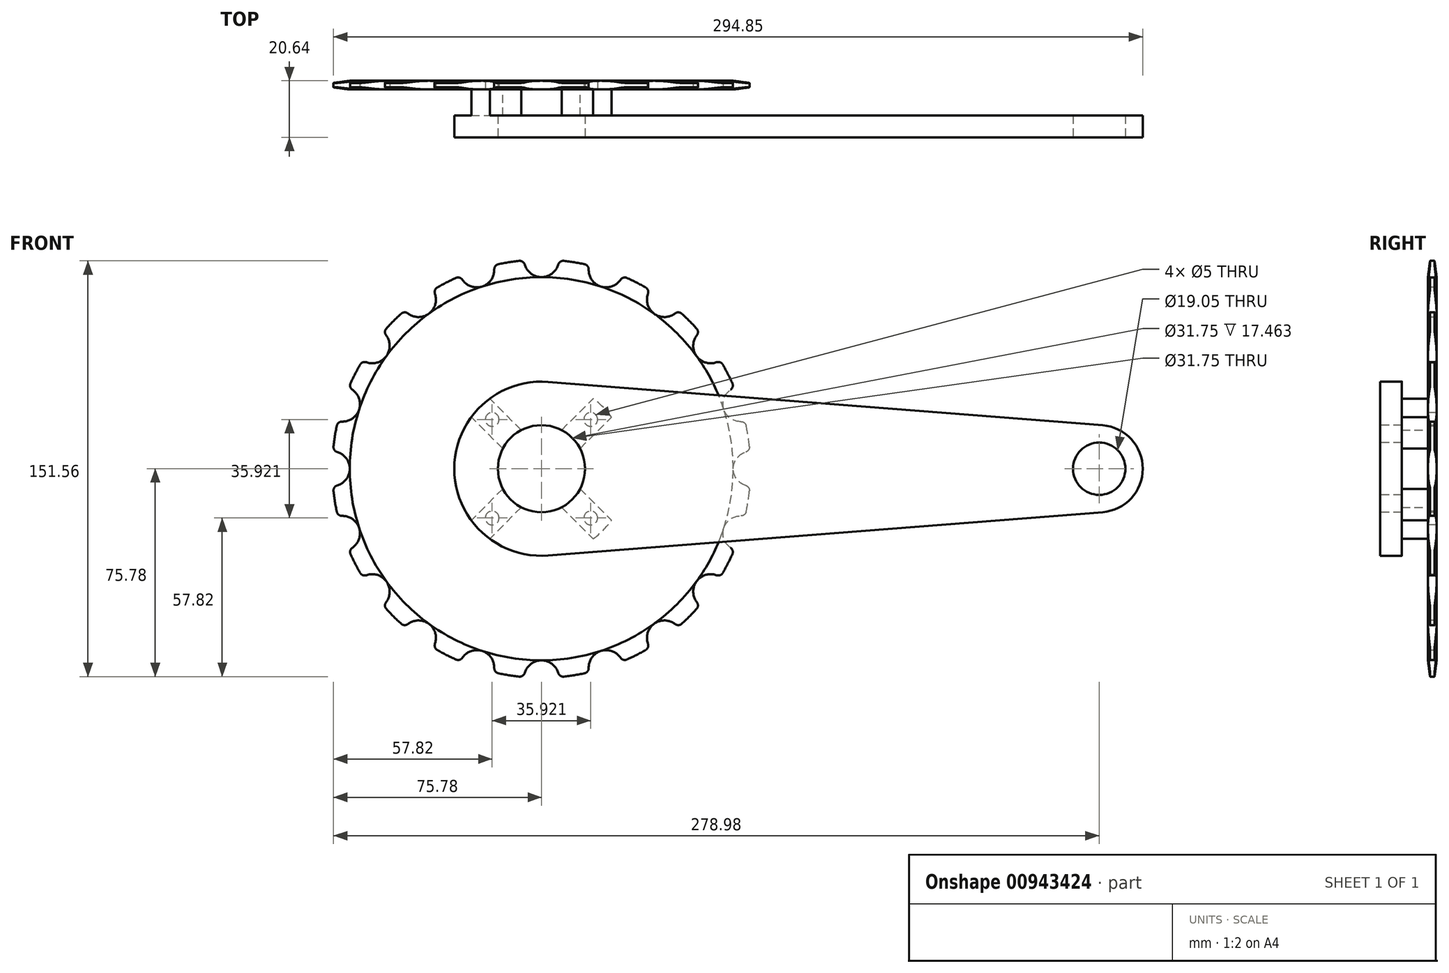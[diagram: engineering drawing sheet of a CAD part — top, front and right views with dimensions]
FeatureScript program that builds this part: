
annotation { "Feature Type Name" : "Feature", "Feature Type Description" : "" }
export const myFeature = defineFeature(function(context is Context, id is Id, definition is map)
    precondition{}
    {
        {
            var Q0;
            Q0=qCreatedBy(makeId("Right.planeOp"),FACE);
            var sketch = newSketch(context, id + "F0", { "sketchPlane" : qUnion([Q0])});
            skLineSegment(sketch, "E0.left", {"start": v(-1.59, 69.85) * mm, "end": v(-1.59, 0) * mm});
            skLineSegment(sketch, "E0.right", {"start": v(1.59, 69.85) * mm, "end": v(1.59, 0) * mm});
            skPoint(sketch, "E0.middle", {"position": v(0, 0) * mm});
            skLineSegment(sketch, "E1", {"start": v(0, 0) * mm, "end": v(-39.14, 0) * mm, "construction": true});
            skLineSegment(sketch, "E2", {"start": v(-1.59, 0) * mm, "end": v(1.59, 0) * mm});
            skLineSegment(sketch, "E3", {"start": v(-1.59, 69.85) * mm, "end": v(-0.8, 76.2) * mm});
            skLineSegment(sketch, "E4", {"start": v(0, 76.2) * mm, "end": v(0, 0) * mm, "construction": true});
            skLineSegment(sketch, "E5.MirrorCS", {"start": v(1.59, 69.85) * mm, "end": v(0.8, 76.2) * mm});
            skLineSegment(sketch, "E6", {"start": v(0.8, 76.2) * mm, "end": v(0, 76.2) * mm});
            skLineSegment(sketch, "E7", {"start": v(-0.8, 76.2) * mm, "end": v(0, 76.2) * mm});
            skSolve(sketch);
        }
        {
            var Q0;
            Q0 = qSketchRegion(id + "F0", true);
            var Q1;
            Q1=sQuery(id+"F0.wireOp",EDGE,"E1");
            revolve(context, id + "F1", {"surfaceOperationType" : NewSurfaceOperationType.NEW, "entities" : qUnion([Q0]), "axis" : qUnion([Q1]), "revolveType" : RevolveType.FULL});
        }
        {
            var Q0;
            Q0=qCreatedBy(makeId("Front.planeOp"),FACE);
            var sketch = newSketch(context, id + "F2", { "sketchPlane" : qUnion([Q0])});
            skCircle(sketch, "E8", {"center": v(0, 76.2) * mm, "radius": 6.35 * mm});
            skCircle(sketch, "E9.1.0", {"center": v(-23.55, 72.47) * mm, "radius": 6.35 * mm});
            skCircle(sketch, "E9.2.0", {"center": v(-44.79, 61.65) * mm, "radius": 6.35 * mm});
            skCircle(sketch, "E9.3.0", {"center": v(-61.65, 44.79) * mm, "radius": 6.35 * mm});
            skCircle(sketch, "E9.4.0", {"center": v(-72.47, 23.55) * mm, "radius": 6.35 * mm});
            skCircle(sketch, "E9.5.0", {"center": v(-76.2, 0) * mm, "radius": 6.35 * mm});
            skCircle(sketch, "E9.6.0", {"center": v(-72.47, -23.55) * mm, "radius": 6.35 * mm});
            skCircle(sketch, "E9.7.0", {"center": v(-61.65, -44.79) * mm, "radius": 6.35 * mm});
            skCircle(sketch, "E9.8.0", {"center": v(-44.79, -61.65) * mm, "radius": 6.35 * mm});
            skCircle(sketch, "E9.9.0", {"center": v(-23.55, -72.47) * mm, "radius": 6.35 * mm});
            skCircle(sketch, "E9.10.0", {"center": v(0, -76.2) * mm, "radius": 6.35 * mm});
            skCircle(sketch, "E9.11.0", {"center": v(23.55, -72.47) * mm, "radius": 6.35 * mm});
            skCircle(sketch, "E9.12.0", {"center": v(44.79, -61.65) * mm, "radius": 6.35 * mm});
            skCircle(sketch, "E9.13.0", {"center": v(61.65, -44.79) * mm, "radius": 6.35 * mm});
            skCircle(sketch, "E9.14.0", {"center": v(72.47, -23.55) * mm, "radius": 6.35 * mm});
            skCircle(sketch, "E9.15.0", {"center": v(76.2, 0) * mm, "radius": 6.35 * mm});
            skCircle(sketch, "E9.16.0", {"center": v(72.47, 23.55) * mm, "radius": 6.35 * mm});
            skCircle(sketch, "E9.17.0", {"center": v(61.65, 44.79) * mm, "radius": 6.35 * mm});
            skCircle(sketch, "E9.18.0", {"center": v(44.79, 61.65) * mm, "radius": 6.35 * mm});
            skCircle(sketch, "E9.19.0", {"center": v(23.55, 72.47) * mm, "radius": 6.35 * mm});
            skPoint(sketch, "E9.center", {"position": v(0, 0) * mm});
            skSolve(sketch);
        }
        {
            var Q0;
            Q0 = qSketchRegion(id + "F2", true);
            extrude(context, id + "F3", {"entities" : qUnion([Q0]), "operationType" : NewBodyOperationType.REMOVE, "endBound" : BoundingType.THROUGH_ALL, "oppositeDirection" : true, "depth" : 25.4 * mm, "offsetDistance" : 25.4 * mm, "hasSecondDirection" : true, "secondDirectionBound" : SecondDirectionBoundingType.THROUGH_ALL, "secondDirectionOppositeDirection" : false, "secondDirectionDepth" : 25.4 * mm});
        }
        {
            var Q0;
            Q0=makeQuery(id+"F3.boolean.opBoolean","INTERSECT",EDGE,{"disambiguationData":[OD(0.0)],"derivedFrom":[makeQuery(id+"F1.opRevolve","SWEPT_FACE",FACE,{"disambiguationData":[OSD([sQuery(id+"F0.wireOp",EDGE,"E6"),sQuery(id+"F0.wireOp",EDGE,"E7")])]}),makeQuery(id+"F3.opExtrude","SWEPT_FACE",FACE,{"disambiguationData":[OSD([sQuery(id+"F2.wireOp",EDGE,"E9.1.0")])]})]});
            var Q1;
            Q1=makeQuery(id+"F3.boolean.opBoolean","INTERSECT",EDGE,{"disambiguationData":[OD(0.0)],"derivedFrom":[makeQuery(id+"F1.opRevolve","SWEPT_FACE",FACE,{"disambiguationData":[OSD([sQuery(id+"F0.wireOp",EDGE,"E6"),sQuery(id+"F0.wireOp",EDGE,"E7")])]}),makeQuery(id+"F3.opExtrude","SWEPT_FACE",FACE,{"disambiguationData":[OSD([sQuery(id+"F2.wireOp",EDGE,"E8")])]})]});
            var Q2;
            Q2=makeQuery(id+"F3.boolean.opBoolean","INTERSECT",EDGE,{"disambiguationData":[OD(1.0)],"derivedFrom":[makeQuery(id+"F1.opRevolve","SWEPT_FACE",FACE,{"disambiguationData":[OSD([sQuery(id+"F0.wireOp",EDGE,"E6"),sQuery(id+"F0.wireOp",EDGE,"E7")])]}),makeQuery(id+"F3.opExtrude","SWEPT_FACE",FACE,{"disambiguationData":[OSD([sQuery(id+"F2.wireOp",EDGE,"E9.1.0")])]})]});
            var Q3;
            Q3=makeQuery(id+"F3.boolean.opBoolean","INTERSECT",EDGE,{"disambiguationData":[OD(0.0)],"derivedFrom":[makeQuery(id+"F1.opRevolve","SWEPT_FACE",FACE,{"disambiguationData":[OSD([sQuery(id+"F0.wireOp",EDGE,"E6"),sQuery(id+"F0.wireOp",EDGE,"E7")])]}),makeQuery(id+"F3.opExtrude","SWEPT_FACE",FACE,{"disambiguationData":[OSD([sQuery(id+"F2.wireOp",EDGE,"E9.2.0")])]})]});
            var Q4;
            Q4=makeQuery(id+"F3.boolean.opBoolean","INTERSECT",EDGE,{"disambiguationData":[OD(0.0)],"derivedFrom":[makeQuery(id+"F1.opRevolve","SWEPT_FACE",FACE,{"disambiguationData":[OSD([sQuery(id+"F0.wireOp",EDGE,"E6"),sQuery(id+"F0.wireOp",EDGE,"E7")])]}),makeQuery(id+"F3.opExtrude","SWEPT_FACE",FACE,{"disambiguationData":[OSD([sQuery(id+"F2.wireOp",EDGE,"E9.19.0")])]})]});
            var Q5;
            Q5=makeQuery(id+"F3.boolean.opBoolean","INTERSECT",EDGE,{"disambiguationData":[OD(1.0)],"derivedFrom":[makeQuery(id+"F1.opRevolve","SWEPT_FACE",FACE,{"disambiguationData":[OSD([sQuery(id+"F0.wireOp",EDGE,"E6"),sQuery(id+"F0.wireOp",EDGE,"E7")])]}),makeQuery(id+"F3.opExtrude","SWEPT_FACE",FACE,{"disambiguationData":[OSD([sQuery(id+"F2.wireOp",EDGE,"E8")])]})]});
            var Q6;
            Q6=makeQuery(id+"F3.boolean.opBoolean","INTERSECT",EDGE,{"disambiguationData":[OD(1.0)],"derivedFrom":[makeQuery(id+"F1.opRevolve","SWEPT_FACE",FACE,{"disambiguationData":[OSD([sQuery(id+"F0.wireOp",EDGE,"E6"),sQuery(id+"F0.wireOp",EDGE,"E7")])]}),makeQuery(id+"F3.opExtrude","SWEPT_FACE",FACE,{"disambiguationData":[OSD([sQuery(id+"F2.wireOp",EDGE,"E9.19.0")])]})]});
            var Q7;
            Q7=makeQuery(id+"F3.boolean.opBoolean","INTERSECT",EDGE,{"disambiguationData":[OD(1.0)],"derivedFrom":[makeQuery(id+"F1.opRevolve","SWEPT_FACE",FACE,{"disambiguationData":[OSD([sQuery(id+"F0.wireOp",EDGE,"E6"),sQuery(id+"F0.wireOp",EDGE,"E7")])]}),makeQuery(id+"F3.opExtrude","SWEPT_FACE",FACE,{"disambiguationData":[OSD([sQuery(id+"F2.wireOp",EDGE,"E9.18.0")])]})]});
            var Q8;
            Q8=makeQuery(id+"F3.boolean.opBoolean","INTERSECT",EDGE,{"disambiguationData":[OD(0.0)],"derivedFrom":[makeQuery(id+"F1.opRevolve","SWEPT_FACE",FACE,{"disambiguationData":[OSD([sQuery(id+"F0.wireOp",EDGE,"E6"),sQuery(id+"F0.wireOp",EDGE,"E7")])]}),makeQuery(id+"F3.opExtrude","SWEPT_FACE",FACE,{"disambiguationData":[OSD([sQuery(id+"F2.wireOp",EDGE,"E9.18.0")])]})]});
            var Q9;
            Q9=makeQuery(id+"F3.boolean.opBoolean","INTERSECT",EDGE,{"disambiguationData":[OD(1.0)],"derivedFrom":[makeQuery(id+"F1.opRevolve","SWEPT_FACE",FACE,{"disambiguationData":[OSD([sQuery(id+"F0.wireOp",EDGE,"E6"),sQuery(id+"F0.wireOp",EDGE,"E7")])]}),makeQuery(id+"F3.opExtrude","SWEPT_FACE",FACE,{"disambiguationData":[OSD([sQuery(id+"F2.wireOp",EDGE,"E9.17.0")])]})]});
            var Q10;
            Q10=makeQuery(id+"F3.boolean.opBoolean","INTERSECT",EDGE,{"disambiguationData":[OD(0.0)],"derivedFrom":[makeQuery(id+"F1.opRevolve","SWEPT_FACE",FACE,{"disambiguationData":[OSD([sQuery(id+"F0.wireOp",EDGE,"E6"),sQuery(id+"F0.wireOp",EDGE,"E7")])]}),makeQuery(id+"F3.opExtrude","SWEPT_FACE",FACE,{"disambiguationData":[OSD([sQuery(id+"F2.wireOp",EDGE,"E9.17.0")])]})]});
            var Q11;
            Q11=makeQuery(id+"F3.boolean.opBoolean","INTERSECT",EDGE,{"disambiguationData":[OD(1.0)],"derivedFrom":[makeQuery(id+"F1.opRevolve","SWEPT_FACE",FACE,{"disambiguationData":[OSD([sQuery(id+"F0.wireOp",EDGE,"E6"),sQuery(id+"F0.wireOp",EDGE,"E7")])]}),makeQuery(id+"F3.opExtrude","SWEPT_FACE",FACE,{"disambiguationData":[OSD([sQuery(id+"F2.wireOp",EDGE,"E9.2.0")])]})]});
            var Q12;
            Q12=makeQuery(id+"F3.boolean.opBoolean","INTERSECT",EDGE,{"disambiguationData":[OD(0.0)],"derivedFrom":[makeQuery(id+"F1.opRevolve","SWEPT_FACE",FACE,{"disambiguationData":[OSD([sQuery(id+"F0.wireOp",EDGE,"E6"),sQuery(id+"F0.wireOp",EDGE,"E7")])]}),makeQuery(id+"F3.opExtrude","SWEPT_FACE",FACE,{"disambiguationData":[OSD([sQuery(id+"F2.wireOp",EDGE,"E9.3.0")])]})]});
            var Q13;
            Q13=makeQuery(id+"F3.boolean.opBoolean","INTERSECT",EDGE,{"disambiguationData":[OD(1.0)],"derivedFrom":[makeQuery(id+"F1.opRevolve","SWEPT_FACE",FACE,{"disambiguationData":[OSD([sQuery(id+"F0.wireOp",EDGE,"E6"),sQuery(id+"F0.wireOp",EDGE,"E7")])]}),makeQuery(id+"F3.opExtrude","SWEPT_FACE",FACE,{"disambiguationData":[OSD([sQuery(id+"F2.wireOp",EDGE,"E9.3.0")])]})]});
            var Q14;
            Q14=makeQuery(id+"F3.boolean.opBoolean","INTERSECT",EDGE,{"disambiguationData":[OD(1.0)],"derivedFrom":[makeQuery(id+"F1.opRevolve","SWEPT_FACE",FACE,{"disambiguationData":[OSD([sQuery(id+"F0.wireOp",EDGE,"E6"),sQuery(id+"F0.wireOp",EDGE,"E7")])]}),makeQuery(id+"F3.opExtrude","SWEPT_FACE",FACE,{"disambiguationData":[OSD([sQuery(id+"F2.wireOp",EDGE,"E9.4.0")])]})]});
            var Q15;
            Q15=makeQuery(id+"F3.boolean.opBoolean","INTERSECT",EDGE,{"disambiguationData":[OD(1.0)],"derivedFrom":[makeQuery(id+"F1.opRevolve","SWEPT_FACE",FACE,{"disambiguationData":[OSD([sQuery(id+"F0.wireOp",EDGE,"E6"),sQuery(id+"F0.wireOp",EDGE,"E7")])]}),makeQuery(id+"F3.opExtrude","SWEPT_FACE",FACE,{"disambiguationData":[OSD([sQuery(id+"F2.wireOp",EDGE,"E9.5.0")])]})]});
            var Q16;
            Q16=makeQuery(id+"F3.boolean.opBoolean","INTERSECT",EDGE,{"disambiguationData":[OD(0.0)],"derivedFrom":[makeQuery(id+"F1.opRevolve","SWEPT_FACE",FACE,{"disambiguationData":[OSD([sQuery(id+"F0.wireOp",EDGE,"E6"),sQuery(id+"F0.wireOp",EDGE,"E7")])]}),makeQuery(id+"F3.opExtrude","SWEPT_FACE",FACE,{"disambiguationData":[OSD([sQuery(id+"F2.wireOp",EDGE,"E9.5.0")])]})]});
            var Q17;
            Q17=makeQuery(id+"F3.boolean.opBoolean","INTERSECT",EDGE,{"disambiguationData":[OD(0.0)],"derivedFrom":[makeQuery(id+"F1.opRevolve","SWEPT_FACE",FACE,{"disambiguationData":[OSD([sQuery(id+"F0.wireOp",EDGE,"E6"),sQuery(id+"F0.wireOp",EDGE,"E7")])]}),makeQuery(id+"F3.opExtrude","SWEPT_FACE",FACE,{"disambiguationData":[OSD([sQuery(id+"F2.wireOp",EDGE,"E9.4.0")])]})]});
            var Q18;
            Q18=makeQuery(id+"F3.boolean.opBoolean","INTERSECT",EDGE,{"disambiguationData":[OD(0.0)],"derivedFrom":[makeQuery(id+"F1.opRevolve","SWEPT_FACE",FACE,{"disambiguationData":[OSD([sQuery(id+"F0.wireOp",EDGE,"E6"),sQuery(id+"F0.wireOp",EDGE,"E7")])]}),makeQuery(id+"F3.opExtrude","SWEPT_FACE",FACE,{"disambiguationData":[OSD([sQuery(id+"F2.wireOp",EDGE,"E9.6.0")])]})]});
            var Q19;
            Q19=makeQuery(id+"F3.boolean.opBoolean","INTERSECT",EDGE,{"disambiguationData":[OD(1.0)],"derivedFrom":[makeQuery(id+"F1.opRevolve","SWEPT_FACE",FACE,{"disambiguationData":[OSD([sQuery(id+"F0.wireOp",EDGE,"E6"),sQuery(id+"F0.wireOp",EDGE,"E7")])]}),makeQuery(id+"F3.opExtrude","SWEPT_FACE",FACE,{"disambiguationData":[OSD([sQuery(id+"F2.wireOp",EDGE,"E9.6.0")])]})]});
            var Q20;
            Q20=makeQuery(id+"F3.boolean.opBoolean","INTERSECT",EDGE,{"disambiguationData":[OD(0.0)],"derivedFrom":[makeQuery(id+"F1.opRevolve","SWEPT_FACE",FACE,{"disambiguationData":[OSD([sQuery(id+"F0.wireOp",EDGE,"E6"),sQuery(id+"F0.wireOp",EDGE,"E7")])]}),makeQuery(id+"F3.opExtrude","SWEPT_FACE",FACE,{"disambiguationData":[OSD([sQuery(id+"F2.wireOp",EDGE,"E9.7.0")])]})]});
            var Q21;
            Q21=makeQuery(id+"F3.boolean.opBoolean","INTERSECT",EDGE,{"disambiguationData":[OD(1.0)],"derivedFrom":[makeQuery(id+"F1.opRevolve","SWEPT_FACE",FACE,{"disambiguationData":[OSD([sQuery(id+"F0.wireOp",EDGE,"E6"),sQuery(id+"F0.wireOp",EDGE,"E7")])]}),makeQuery(id+"F3.opExtrude","SWEPT_FACE",FACE,{"disambiguationData":[OSD([sQuery(id+"F2.wireOp",EDGE,"E9.7.0")])]})]});
            var Q22;
            Q22=makeQuery(id+"F3.boolean.opBoolean","INTERSECT",EDGE,{"disambiguationData":[OD(0.0)],"derivedFrom":[makeQuery(id+"F1.opRevolve","SWEPT_FACE",FACE,{"disambiguationData":[OSD([sQuery(id+"F0.wireOp",EDGE,"E6"),sQuery(id+"F0.wireOp",EDGE,"E7")])]}),makeQuery(id+"F3.opExtrude","SWEPT_FACE",FACE,{"disambiguationData":[OSD([sQuery(id+"F2.wireOp",EDGE,"E9.8.0")])]})]});
            var Q23;
            Q23=makeQuery(id+"F3.boolean.opBoolean","INTERSECT",EDGE,{"disambiguationData":[OD(1.0)],"derivedFrom":[makeQuery(id+"F1.opRevolve","SWEPT_FACE",FACE,{"disambiguationData":[OSD([sQuery(id+"F0.wireOp",EDGE,"E6"),sQuery(id+"F0.wireOp",EDGE,"E7")])]}),makeQuery(id+"F3.opExtrude","SWEPT_FACE",FACE,{"disambiguationData":[OSD([sQuery(id+"F2.wireOp",EDGE,"E9.8.0")])]})]});
            var Q24;
            Q24=makeQuery(id+"F3.boolean.opBoolean","INTERSECT",EDGE,{"disambiguationData":[OD(0.0)],"derivedFrom":[makeQuery(id+"F1.opRevolve","SWEPT_FACE",FACE,{"disambiguationData":[OSD([sQuery(id+"F0.wireOp",EDGE,"E6"),sQuery(id+"F0.wireOp",EDGE,"E7")])]}),makeQuery(id+"F3.opExtrude","SWEPT_FACE",FACE,{"disambiguationData":[OSD([sQuery(id+"F2.wireOp",EDGE,"E9.9.0")])]})]});
            var Q25;
            Q25=makeQuery(id+"F3.boolean.opBoolean","INTERSECT",EDGE,{"disambiguationData":[OD(1.0)],"derivedFrom":[makeQuery(id+"F1.opRevolve","SWEPT_FACE",FACE,{"disambiguationData":[OSD([sQuery(id+"F0.wireOp",EDGE,"E6"),sQuery(id+"F0.wireOp",EDGE,"E7")])]}),makeQuery(id+"F3.opExtrude","SWEPT_FACE",FACE,{"disambiguationData":[OSD([sQuery(id+"F2.wireOp",EDGE,"E9.9.0")])]})]});
            var Q26;
            Q26=makeQuery(id+"F3.boolean.opBoolean","INTERSECT",EDGE,{"disambiguationData":[OD(0.0)],"derivedFrom":[makeQuery(id+"F1.opRevolve","SWEPT_FACE",FACE,{"disambiguationData":[OSD([sQuery(id+"F0.wireOp",EDGE,"E6"),sQuery(id+"F0.wireOp",EDGE,"E7")])]}),makeQuery(id+"F3.opExtrude","SWEPT_FACE",FACE,{"disambiguationData":[OSD([sQuery(id+"F2.wireOp",EDGE,"E9.10.0")])]})]});
            var Q27;
            Q27=makeQuery(id+"F3.boolean.opBoolean","INTERSECT",EDGE,{"disambiguationData":[OD(1.0)],"derivedFrom":[makeQuery(id+"F1.opRevolve","SWEPT_FACE",FACE,{"disambiguationData":[OSD([sQuery(id+"F0.wireOp",EDGE,"E6"),sQuery(id+"F0.wireOp",EDGE,"E7")])]}),makeQuery(id+"F3.opExtrude","SWEPT_FACE",FACE,{"disambiguationData":[OSD([sQuery(id+"F2.wireOp",EDGE,"E9.10.0")])]})]});
            var Q28;
            Q28=makeQuery(id+"F3.boolean.opBoolean","INTERSECT",EDGE,{"disambiguationData":[OD(0.0)],"derivedFrom":[makeQuery(id+"F1.opRevolve","SWEPT_FACE",FACE,{"disambiguationData":[OSD([sQuery(id+"F0.wireOp",EDGE,"E6"),sQuery(id+"F0.wireOp",EDGE,"E7")])]}),makeQuery(id+"F3.opExtrude","SWEPT_FACE",FACE,{"disambiguationData":[OSD([sQuery(id+"F2.wireOp",EDGE,"E9.11.0")])]})]});
            var Q29;
            Q29=makeQuery(id+"F3.boolean.opBoolean","INTERSECT",EDGE,{"disambiguationData":[OD(1.0)],"derivedFrom":[makeQuery(id+"F1.opRevolve","SWEPT_FACE",FACE,{"disambiguationData":[OSD([sQuery(id+"F0.wireOp",EDGE,"E6"),sQuery(id+"F0.wireOp",EDGE,"E7")])]}),makeQuery(id+"F3.opExtrude","SWEPT_FACE",FACE,{"disambiguationData":[OSD([sQuery(id+"F2.wireOp",EDGE,"E9.11.0")])]})]});
            var Q30;
            Q30=makeQuery(id+"F3.boolean.opBoolean","INTERSECT",EDGE,{"disambiguationData":[OD(0.0)],"derivedFrom":[makeQuery(id+"F1.opRevolve","SWEPT_FACE",FACE,{"disambiguationData":[OSD([sQuery(id+"F0.wireOp",EDGE,"E6"),sQuery(id+"F0.wireOp",EDGE,"E7")])]}),makeQuery(id+"F3.opExtrude","SWEPT_FACE",FACE,{"disambiguationData":[OSD([sQuery(id+"F2.wireOp",EDGE,"E9.12.0")])]})]});
            var Q31;
            Q31=makeQuery(id+"F3.boolean.opBoolean","INTERSECT",EDGE,{"disambiguationData":[OD(1.0)],"derivedFrom":[makeQuery(id+"F1.opRevolve","SWEPT_FACE",FACE,{"disambiguationData":[OSD([sQuery(id+"F0.wireOp",EDGE,"E6"),sQuery(id+"F0.wireOp",EDGE,"E7")])]}),makeQuery(id+"F3.opExtrude","SWEPT_FACE",FACE,{"disambiguationData":[OSD([sQuery(id+"F2.wireOp",EDGE,"E9.12.0")])]})]});
            var Q32;
            Q32=makeQuery(id+"F3.boolean.opBoolean","INTERSECT",EDGE,{"disambiguationData":[OD(0.0)],"derivedFrom":[makeQuery(id+"F1.opRevolve","SWEPT_FACE",FACE,{"disambiguationData":[OSD([sQuery(id+"F0.wireOp",EDGE,"E6"),sQuery(id+"F0.wireOp",EDGE,"E7")])]}),makeQuery(id+"F3.opExtrude","SWEPT_FACE",FACE,{"disambiguationData":[OSD([sQuery(id+"F2.wireOp",EDGE,"E9.13.0")])]})]});
            var Q33;
            Q33=makeQuery(id+"F3.boolean.opBoolean","INTERSECT",EDGE,{"disambiguationData":[OD(0.0)],"derivedFrom":[makeQuery(id+"F1.opRevolve","SWEPT_FACE",FACE,{"disambiguationData":[OSD([sQuery(id+"F0.wireOp",EDGE,"E6"),sQuery(id+"F0.wireOp",EDGE,"E7")])]}),makeQuery(id+"F3.opExtrude","SWEPT_FACE",FACE,{"disambiguationData":[OSD([sQuery(id+"F2.wireOp",EDGE,"E9.14.0")])]})]});
            var Q34;
            Q34=makeQuery(id+"F3.boolean.opBoolean","INTERSECT",EDGE,{"disambiguationData":[OD(1.0)],"derivedFrom":[makeQuery(id+"F1.opRevolve","SWEPT_FACE",FACE,{"disambiguationData":[OSD([sQuery(id+"F0.wireOp",EDGE,"E6"),sQuery(id+"F0.wireOp",EDGE,"E7")])]}),makeQuery(id+"F3.opExtrude","SWEPT_FACE",FACE,{"disambiguationData":[OSD([sQuery(id+"F2.wireOp",EDGE,"E9.13.0")])]})]});
            var Q35;
            Q35=makeQuery(id+"F3.boolean.opBoolean","INTERSECT",EDGE,{"disambiguationData":[OD(0.0)],"derivedFrom":[makeQuery(id+"F1.opRevolve","SWEPT_FACE",FACE,{"disambiguationData":[OSD([sQuery(id+"F0.wireOp",EDGE,"E6"),sQuery(id+"F0.wireOp",EDGE,"E7")])]}),makeQuery(id+"F3.opExtrude","SWEPT_FACE",FACE,{"disambiguationData":[OSD([sQuery(id+"F2.wireOp",EDGE,"E9.16.0")])]})]});
            var Q36;
            Q36=makeQuery(id+"F3.boolean.opBoolean","INTERSECT",EDGE,{"disambiguationData":[OD(1.0)],"derivedFrom":[makeQuery(id+"F1.opRevolve","SWEPT_FACE",FACE,{"disambiguationData":[OSD([sQuery(id+"F0.wireOp",EDGE,"E6"),sQuery(id+"F0.wireOp",EDGE,"E7")])]}),makeQuery(id+"F3.opExtrude","SWEPT_FACE",FACE,{"disambiguationData":[OSD([sQuery(id+"F2.wireOp",EDGE,"E9.15.0")])]})]});
            var Q37;
            Q37=makeQuery(id+"F3.boolean.opBoolean","INTERSECT",EDGE,{"disambiguationData":[OD(0.0)],"derivedFrom":[makeQuery(id+"F1.opRevolve","SWEPT_FACE",FACE,{"disambiguationData":[OSD([sQuery(id+"F0.wireOp",EDGE,"E6"),sQuery(id+"F0.wireOp",EDGE,"E7")])]}),makeQuery(id+"F3.opExtrude","SWEPT_FACE",FACE,{"disambiguationData":[OSD([sQuery(id+"F2.wireOp",EDGE,"E9.15.0")])]})]});
            var Q38;
            Q38=makeQuery(id+"F3.boolean.opBoolean","INTERSECT",EDGE,{"disambiguationData":[OD(1.0)],"derivedFrom":[makeQuery(id+"F1.opRevolve","SWEPT_FACE",FACE,{"disambiguationData":[OSD([sQuery(id+"F0.wireOp",EDGE,"E6"),sQuery(id+"F0.wireOp",EDGE,"E7")])]}),makeQuery(id+"F3.opExtrude","SWEPT_FACE",FACE,{"disambiguationData":[OSD([sQuery(id+"F2.wireOp",EDGE,"E9.14.0")])]})]});
            var Q39;
            Q39=makeQuery(id+"F3.boolean.opBoolean","INTERSECT",EDGE,{"disambiguationData":[OD(1.0)],"derivedFrom":[makeQuery(id+"F1.opRevolve","SWEPT_FACE",FACE,{"disambiguationData":[OSD([sQuery(id+"F0.wireOp",EDGE,"E6"),sQuery(id+"F0.wireOp",EDGE,"E7")])]}),makeQuery(id+"F3.opExtrude","SWEPT_FACE",FACE,{"disambiguationData":[OSD([sQuery(id+"F2.wireOp",EDGE,"E9.16.0")])]})]});
            fillet(context, id + "F4", {"entities" : qUnion([Q0, Q1, Q2, Q3, Q4, Q5, Q6, Q7, Q8, Q9, Q10, Q11, Q12, Q13, Q14, Q15, Q16, Q17, Q18, Q19, Q20, Q21, Q22, Q23, Q24, Q25, Q26, Q27, Q28, Q29, Q30, Q31, Q32, Q33, Q34, Q35, Q36, Q37, Q38, Q39]), "radius" : 1.9 * mm, "tangentPropagation" : true, "allowEdgeOverflow" : false});
        }
        {
            var Q0;
            Q0=qCreatedBy(makeId("Front.planeOp"),FACE);
            var sketch = newSketch(context, id + "F5", { "sketchPlane" : qUnion([Q0])});
            skCircle(sketch, "E10", {"center": v(0, 0) * mm, "radius": 15.88 * mm});
            skSolve(sketch);
        }
        {
            var Q0;
            Q0 = qSketchRegion(id + "F5", true);
            extrude(context, id + "F6", {"entities" : qUnion([Q0]), "operationType" : NewBodyOperationType.REMOVE, "endBound" : BoundingType.THROUGH_ALL, "oppositeDirection" : true, "depth" : 25.4 * mm, "offsetDistance" : 25.4 * mm, "hasSecondDirection" : true, "secondDirectionBound" : SecondDirectionBoundingType.THROUGH_ALL, "secondDirectionOppositeDirection" : false, "secondDirectionDepth" : 25.4 * mm});
        }
        {
            var Q0;
            Q0=makeQuery(id+"F1.opRevolve","SWEPT_FACE",FACE,{"disambiguationData":[OSD([sQuery(id+"F0.wireOp",EDGE,"E0.left")])]});
            var sketch = newSketch(context, id + "F7", { "sketchPlane" : qUnion([Q0])});
            skCircle(sketch, "E11", {"center": v(0, 0) * mm, "radius": 25.4 * mm, "construction": true});
            skPoint(sketch, "E12", {"position": v(-17.96, 17.96) * mm});
            skPoint(sketch, "E13", {"position": v(17.96, -17.96) * mm});
            skPoint(sketch, "E14", {"position": v(-17.96, -17.96) * mm});
            skPoint(sketch, "E15", {"position": v(17.96, 17.96) * mm});
            skLineSegment(sketch, "E16", {"start": v(17.96, 17.96) * mm, "end": v(0, 0) * mm});
            skLineSegment(sketch, "E17", {"start": v(-17.96, -17.96) * mm, "end": v(0, 0) * mm});
            skLineSegment(sketch, "E18", {"start": v(17.96, -17.96) * mm, "end": v(0, 0) * mm});
            skLineSegment(sketch, "E19", {"start": v(-17.96, 17.96) * mm, "end": v(0, 0) * mm});
            skSolve(sketch);
        }
        {
            var Q0;
            Q0=sQuery(id+"F7.wireOp",VERTEX,"E12");
            var Q1;
            Q1=sQuery(id+"F7.wireOp",VERTEX,"E15");
            var Q2;
            Q2=sQuery(id+"F7.wireOp",VERTEX,"E13");
            var Q3;
            Q3=sQuery(id+"F7.wireOp",VERTEX,"E14");
            var Q4;
            Q4=makeQuery(id+"F1.opRevolve","SWEPT_BODY",BODY,{"disambiguationData":[OSD([sQuery(id+"F0.wireOp",EDGE,"E0.left"),sQuery(id+"F0.wireOp",EDGE,"E0.right"),sQuery(id+"F0.wireOp",EDGE,"E2"),sQuery(id+"F0.wireOp",EDGE,"E3"),sQuery(id+"F0.wireOp",EDGE,"E5.MirrorCS"),sQuery(id+"F0.wireOp",EDGE,"E6"),sQuery(id+"F0.wireOp",EDGE,"E7")])]});
            hole(context, id + "F8", {"style" : HoleStyle.SIMPLE, "endStyle" : HoleEndStyle.THROUGH, "standardTappedOrClearance" : lookupTablePath({ "standard" : "ISO", "engagement" : "75%", "pitch" : "1 mm", "size" : "M6", "type" : "Tapped" }), "standardBlindInLast" : lookupTablePath({ "standard" : "ISO", "fit" : "Normal", "engagement" : "75%", "pitch" : "1 mm", "size" : "M6", "type" : "Clearance & tapped" }), "holeDiameter" : 5 * mm, "majorDiameter" : 6 * mm, "showTappedDepth" : true, "isTappedThrough" : true, "tappedDepth" : 12.7 * mm, "tapClearance" : 3, "locations" : qUnion([Q0, Q1, Q2, Q3]), "scope" : qUnion([Q4])});
        }
        {
            var Q0;
            Q0=qCreatedBy(makeId("Front.planeOp"),FACE);
            cPlane(context, id + "F9", {"entities" : qUnion([Q0]), "cplaneType" : CPlaneType.OFFSET, "offset" : 19.05 * mm, "width" : 152.4 * mm, "height" : 152.4 * mm});
        }
        {
            var Q0;
            Q0=qCreatedBy(id+"F9.planeOp",FACE);
            var sketch = newSketch(context, id + "F10", { "sketchPlane" : qUnion([Q0])});
            skCircle(sketch, "E20", {"center": v(0, 0) * mm, "radius": 31.75 * mm});
            skCircle(sketch, "E21", {"center": v(0, 0) * mm, "radius": 15.88 * mm});
            skCircle(sketch, "E22", {"center": v(203.2, 0) * mm, "radius": 9.53 * mm});
            skCircle(sketch, "E23", {"center": v(203.2, 0) * mm, "radius": 15.88 * mm});
            skLineSegment(sketch, "E24", {"start": v(2.48, 31.65) * mm, "end": v(204.44, 15.83) * mm});
            skLineSegment(sketch, "E25", {"start": v(204.44, -15.83) * mm, "end": v(2.48, -31.65) * mm});
            skSolve(sketch);
        }
        {
            var Q0;
            Q0=makeQuery(id+"F10.imprint","IMPRINT",FACE,{"disambiguationData":[TD([[makeQuery(id+"F10.imprint","IMPRINT",EDGE,{"derivedFrom":sQuery(id+"F10.wireOp",EDGE,"E20")}),1.0]])]});
            var Q1;
            {var subQ0=sQuery(id+"F10.wireOp",EDGE,"E24");Q1=makeQuery(id+"F10.imprint","IMPRINT",FACE,{"disambiguationData":[TD([[makeQuery(id+"F10.imprint","IMPRINT",EDGE,{"derivedFrom":subQ0}),-1.0]])]});}
            var Q2;
            Q2=makeQuery(id+"F10.imprint","IMPRINT",FACE,{"disambiguationData":[TD([[makeQuery(id+"F10.imprint","IMPRINT",EDGE,{"derivedFrom":sQuery(id+"F10.wireOp",EDGE,"E22")}),-1.0]])]});
            var Q3;
            Q3=makeQuery(id+"F1.opRevolve","SWEPT_FACE",FACE,{"disambiguationData":[OSD([sQuery(id+"F0.wireOp",EDGE,"E0.left")])]});
            var Q4;
            Q4=makeQuery(id+"F1.opRevolve","SWEPT_BODY",BODY,{"disambiguationData":[OSD([sQuery(id+"F0.wireOp",EDGE,"E0.left"),sQuery(id+"F0.wireOp",EDGE,"E0.right"),sQuery(id+"F0.wireOp",EDGE,"E2"),sQuery(id+"F0.wireOp",EDGE,"E3"),sQuery(id+"F0.wireOp",EDGE,"E5.MirrorCS"),sQuery(id+"F0.wireOp",EDGE,"E6"),sQuery(id+"F0.wireOp",EDGE,"E7")])]});
            extrude(context, id + "F11", {"entities" : qUnion([Q0, Q1, Q2]), "endBound" : BoundingType.UP_TO_SURFACE, "oppositeDirection" : true, "depth" : 25.4 * mm, "endBoundEntityFace" : qUnion([Q3]), "endBoundEntityBody" : qUnion([Q4]), "offsetDistance" : 25.4 * mm});
        }
        {
            var Q0;
            Q0=makeQuery(id+"F11.opExtrude","CAP_FACE",FACE,{"disambiguationData":[OSD([sQuery(id+"F10.wireOp",EDGE,"E20"),sQuery(id+"F10.wireOp",EDGE,"E21"),sQuery(id+"F10.wireOp",EDGE,"E22"),sQuery(id+"F10.wireOp",EDGE,"E23"),sQuery(id+"F10.wireOp",EDGE,"E24"),sQuery(id+"F10.wireOp",EDGE,"E25")])],"isStart":false});
            var sketch = newSketch(context, id + "F12", { "sketchPlane" : qUnion([Q0])});
            skLineSegment(sketch, "E26.0.0", {"start": v(-204.44, 15.83) * mm, "end": v(-2.48, 31.65) * mm});
            skArc(sketch, "E26.0.1", {"start": v(-2.48, 31.65) * mm, "mid": v(-31.75, 0) * mm, "end": v(-2.48, -31.65) * mm});
            skLineSegment(sketch, "E26.0.2", {"start": v(-2.48, -31.65) * mm, "end": v(-204.44, -15.83) * mm});
            skArc(sketch, "E26.0.3", {"start": v(-204.44, -15.83) * mm, "mid": v(-187.33, 0) * mm, "end": v(-204.44, 15.83) * mm});
            skArc(sketch, "E27.0.0", {"start": v(-2.48, -31.65) * mm, "mid": v(31.75, 0) * mm, "end": v(-2.48, 31.65) * mm});
            skLineSegment(sketch, "E27.0.1", {"start": v(-2.48, 31.65) * mm, "end": v(-204.44, 15.83) * mm});
            skArc(sketch, "E27.0.2", {"start": v(-204.44, 15.83) * mm, "mid": v(-219.08, 0) * mm, "end": v(-204.44, -15.83) * mm});
            skLineSegment(sketch, "E27.0.3", {"start": v(-204.44, -15.83) * mm, "end": v(-2.48, -31.65) * mm});
            skSolve(sketch);
        }
        {
            var Q0;
            Q0=makeQuery(id+"F12.imprint","IMPRINT",FACE,{"disambiguationData":[TD([[makeQuery(id+"F12.imprint","IMPRINT",EDGE,{"derivedFrom":makeQuery(id+"F11.opExtrude","CAP_EDGE",EDGE,{"disambiguationData":[OSD([sQuery(id+"F10.wireOp",EDGE,"E21")])],"isStart":false})}),1.0]])]});
            var Q1;
            Q1=makeQuery(id+"F12.imprint","IMPRINT",FACE,{"disambiguationData":[TD([[makeQuery(id+"F12.imprint","IMPRINT",EDGE,{"derivedFrom":makeQuery(id+"F11.opExtrude","CAP_EDGE",EDGE,{"disambiguationData":[OSD([sQuery(id+"F10.wireOp",EDGE,"E22")])],"isStart":false})}),1.0]])]});
            var Q2;
            Q2=makeQuery(id+"F12.imprint","IMPRINT",FACE,{"disambiguationData":[TD([[makeQuery(id+"F12.imprint","IMPRINT",EDGE,{"derivedFrom":sQuery(id+"F12.wireOp",EDGE,"E26.0.1")}),-1.0]])]});
            var Q3;
            Q3=makeQuery(id+"F12.imprint","IMPRINT",FACE,{"disambiguationData":[TD([[makeQuery(id+"F12.imprint","IMPRINT",EDGE,{"derivedFrom":sQuery(id+"F12.wireOp",EDGE,"E26.0.3")}),1.0]])]});
            extrude(context, id + "F13", {"entities" : qUnion([Q0, Q1, Q2, Q3]), "operationType" : NewBodyOperationType.REMOVE, "oppositeDirection" : true, "depth" : 9.52 * mm, "offsetDistance" : 25.4 * mm});
        }
        {
            var Q0;
            Q0=makeQuery(id+"F11.opExtrude","CAP_FACE",FACE,{"disambiguationData":[OSD([sQuery(id+"F10.wireOp",EDGE,"E20"),sQuery(id+"F10.wireOp",EDGE,"E21"),sQuery(id+"F10.wireOp",EDGE,"E22"),sQuery(id+"F10.wireOp",EDGE,"E23"),sQuery(id+"F10.wireOp",EDGE,"E24"),sQuery(id+"F10.wireOp",EDGE,"E25")])],"isStart":false});
            var sketch = newSketch(context, id + "F14", { "sketchPlane" : qUnion([Q0])});
            skCircle(sketch, "E28.0", {"center": v(0, 0) * mm, "radius": 15.88 * mm});
            skCircle(sketch, "E28.1", {"center": v(0, 0) * mm, "radius": 31.75 * mm});
            skLineSegment(sketch, "E29", {"start": v(11.23, 11.23) * mm, "end": v(0, 0) * mm, "construction": true});
            skLineSegment(sketch, "E30", {"start": v(11.23, -11.23) * mm, "end": v(0, 0) * mm, "construction": true});
            skLineSegment(sketch, "E31", {"start": v(-11.23, 11.23) * mm, "end": v(0, 0) * mm, "construction": true});
            skLineSegment(sketch, "E32", {"start": v(-11.23, -11.23) * mm, "end": v(0, 0) * mm, "construction": true});
            skLineSegment(sketch, "E33", {"start": v(-7.34, 14.08) * mm, "end": v(-18.83, 25.56) * mm});
            skLineSegment(sketch, "E34", {"start": v(-14.08, 7.34) * mm, "end": v(-25.56, 18.83) * mm});
            skLineSegment(sketch, "E35.1.0", {"start": v(-14.08, -7.34) * mm, "end": v(-25.56, -18.83) * mm});
            skLineSegment(sketch, "E35.1.1", {"start": v(-7.34, -14.08) * mm, "end": v(-18.83, -25.56) * mm});
            skLineSegment(sketch, "E35.2.0", {"start": v(7.34, -14.08) * mm, "end": v(18.83, -25.56) * mm});
            skLineSegment(sketch, "E35.2.1", {"start": v(14.08, -7.34) * mm, "end": v(25.56, -18.83) * mm});
            skLineSegment(sketch, "E35.3.0", {"start": v(14.08, 7.34) * mm, "end": v(25.56, 18.83) * mm});
            skLineSegment(sketch, "E35.3.1", {"start": v(7.34, 14.08) * mm, "end": v(18.83, 25.56) * mm});
            skSolve(sketch);
        }
        {
            var Q0;
            {var subQ0=sQuery(id+"F14.wireOp",EDGE,"E33");Q0=makeQuery(id+"F14.imprint","IMPRINT",FACE,{"disambiguationData":[TD([[makeQuery(id+"F14.imprint","IMPRINT",EDGE,{"derivedFrom":subQ0}),-1.0]])]});}
            var Q1;
            {var subQ0=sQuery(id+"F14.wireOp",EDGE,"E34");Q1=makeQuery(id+"F14.imprint","IMPRINT",FACE,{"disambiguationData":[TD([[makeQuery(id+"F14.imprint","IMPRINT",EDGE,{"derivedFrom":subQ0}),1.0]])]});}
            var Q2;
            {var subQ0=sQuery(id+"F14.wireOp",EDGE,"E35.1.1");Q2=makeQuery(id+"F14.imprint","IMPRINT",FACE,{"disambiguationData":[TD([[makeQuery(id+"F14.imprint","IMPRINT",EDGE,{"derivedFrom":subQ0}),1.0]])]});}
            var Q3;
            {var subQ0=sQuery(id+"F14.wireOp",EDGE,"E35.2.1");Q3=makeQuery(id+"F14.imprint","IMPRINT",FACE,{"disambiguationData":[TD([[makeQuery(id+"F14.imprint","IMPRINT",EDGE,{"derivedFrom":subQ0}),1.0]])]});}
            var Q4;
            Q4=makeQuery(id+"F13.boolean.opBoolean","COPY",FACE,{"derivedFrom":makeQuery(id+"F13.opExtrude","CAP_FACE",FACE,{"disambiguationData":[OSD([sQuery(id+"F12.wireOp",EDGE,"E26.0.1"),sQuery(id+"F12.wireOp",EDGE,"E27.0.1"),sQuery(id+"F12.wireOp",EDGE,"E27.0.2"),sQuery(id+"F12.wireOp",EDGE,"E27.0.3")])],"isStart":false})});
            extrude(context, id + "F15", {"entities" : qUnion([Q0, Q1, Q2, Q3]), "operationType" : NewBodyOperationType.REMOVE, "endBound" : BoundingType.UP_TO_SURFACE, "oppositeDirection" : true, "depth" : 25.4 * mm, "endBoundEntityFace" : qUnion([Q4]), "offsetDistance" : 25.4 * mm});
        }
    });
